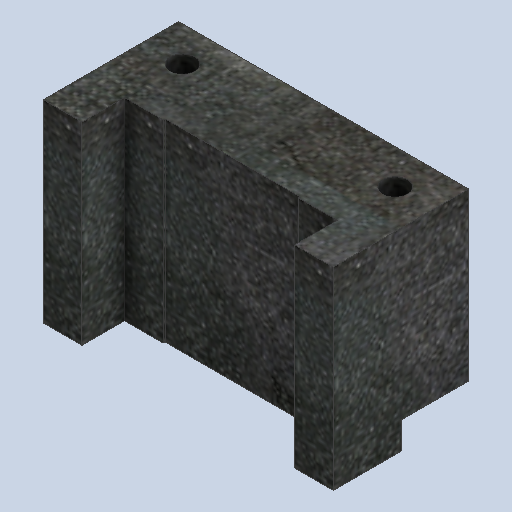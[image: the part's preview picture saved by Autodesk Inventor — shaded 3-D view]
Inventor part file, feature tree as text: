
AUTODESK INVENTOR PART (.ipt)
format: ipt  version: 2023.2 (Build 272271000, 271)  size: 438,784 bytes
history: native  units: mm
features: extrude x4, sketch x4
ambient origin geometry x8: Origin, YZ Plane, XZ Plane, XY Plane, X Axis, Y Axis, Z Axis, Center Point
bodies: Solid1 (feature_tree)
feature tree (8):
  extrude  "Extrusion1"  Depth=35.0mm
  extrude  "Extrusion2"  Depth=11.0mm
  extrude  "Extrusion3"  Depth=35.0mm
  extrude  "Extrusion4"  Depth=11.0mm
  sketch  "Sketch1"  dims[d0=75.0mm d1=35.0mm]
  sketch  "Sketch2"  dims[d2=10.0mm d3=11.0mm]
  sketch  "Sketch3"  dims[d4=10.0mm d5=35.0mm]
  sketch  "Sketch5"  dims[d6=10.0mm d7=11.0mm d8=11.0mm d9=26.0mm d10=11.0mm d11=24.0mm d12=27.5mm d13=27.5mm d14=7.0mm d15=0.0mm d17=6.4mm d24=6.4mm d25=27.5mm d26=27.5mm d27=26.0mm d28=26.0mm d29=11.0mm d30=24.0mm d31=13.0mm d32=0.0mm d33=6.4mm d34=6.4mm d35=26.0mm d36=27.5mm d37=27.5mm d38=23.0mm d39=0.0mm d41=16.0mm d42=7.0mm d43=0.0mm]
